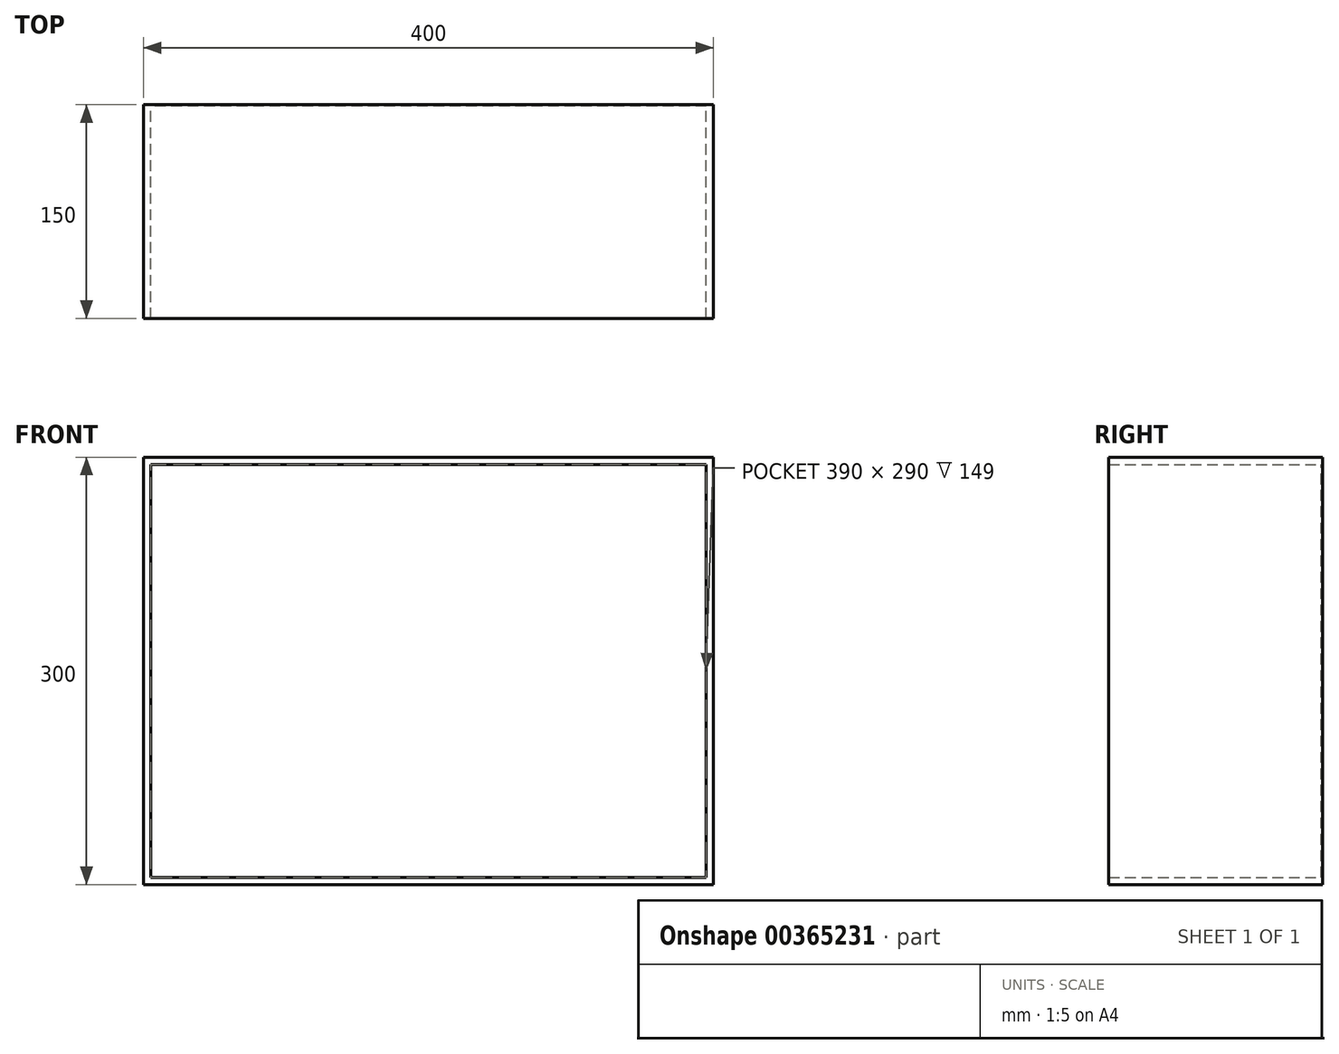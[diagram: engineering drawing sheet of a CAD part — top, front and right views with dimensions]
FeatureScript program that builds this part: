
annotation { "Feature Type Name" : "Feature", "Feature Type Description" : "" }
export const myFeature = defineFeature(function(context is Context, id is Id, definition is map)
    precondition{}
    {
        {
            var Q0;
            Q0=qCreatedBy(makeId("Front.planeOp"),FACE);
            var sketch = newSketch(context, id + "F0", { "sketchPlane" : qUnion([Q0])});
            skLineSegment(sketch, "E0.bottom", {"start": v(200, -150) * mm, "end": v(-200, -150) * mm});
            skLineSegment(sketch, "E0.top", {"start": v(200, 150) * mm, "end": v(-200, 150) * mm});
            skLineSegment(sketch, "E0.left", {"start": v(200, -150) * mm, "end": v(200, 150) * mm});
            skLineSegment(sketch, "E0.right", {"start": v(-200, -150) * mm, "end": v(-200, 150) * mm});
            skPoint(sketch, "E0.middle", {"position": v(0, 0) * mm});
            skLineSegment(sketch, "E1.0", {"start": v(195, 145) * mm, "end": v(-195, 145) * mm});
            skLineSegment(sketch, "E1.1", {"start": v(195, -145) * mm, "end": v(195, 145) * mm});
            skLineSegment(sketch, "E1.2", {"start": v(195, -145) * mm, "end": v(-195, -145) * mm});
            skLineSegment(sketch, "E1.3", {"start": v(-195, -145) * mm, "end": v(-195, 145) * mm});
            skSolve(sketch);
        }
        {
            var Q0;
            Q0=makeQuery(id+"F0.imprint","IMPRINT",FACE,{"disambiguationData":[TD([[makeQuery(id+"F0.imprint","IMPRINT",EDGE,{"derivedFrom":sQuery(id+"F0.wireOp",EDGE,"E0.bottom")}),-1.0]])]});
            extrude(context, id + "F1", {"entities" : qUnion([Q0]), "depth" : 150 * mm});
        }
        {
            var Q0;
            Q0=makeQuery(id+"F1.opExtrude","CAP_FACE",FACE,{"disambiguationData":[OSD([sQuery(id+"F0.wireOp",EDGE,"E0.bottom"),sQuery(id+"F0.wireOp",EDGE,"E0.top"),sQuery(id+"F0.wireOp",EDGE,"E0.left"),sQuery(id+"F0.wireOp",EDGE,"E0.right"),sQuery(id+"F0.wireOp",EDGE,"E1.0"),sQuery(id+"F0.wireOp",EDGE,"E1.1"),sQuery(id+"F0.wireOp",EDGE,"E1.2"),sQuery(id+"F0.wireOp",EDGE,"E1.3")])],"isStart":true});
            var sketch = newSketch(context, id + "F2", { "sketchPlane" : qUnion([Q0])});
            skLineSegment(sketch, "E2.0", {"start": v(-195, 145) * mm, "end": v(195, 145) * mm});
            skLineSegment(sketch, "E3.0", {"start": v(-195, -145) * mm, "end": v(195, -145) * mm});
            skLineSegment(sketch, "E4", {"start": v(-195, 145) * mm, "end": v(-195, -145) * mm});
            skLineSegment(sketch, "E5", {"start": v(195, 145) * mm, "end": v(195, -145) * mm});
            skSolve(sketch);
        }
        {
            var Q0;
            Q0 = qSketchRegion(id + "F2", true);
            extrude(context, id + "F3", {"entities" : qUnion([Q0]), "operationType" : NewBodyOperationType.ADD, "oppositeDirection" : true, "depth" : 1 * mm});
        }
    });
